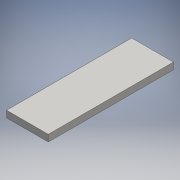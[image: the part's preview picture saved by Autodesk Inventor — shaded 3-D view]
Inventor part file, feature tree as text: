
AUTODESK INVENTOR PART (.ipt)
format: ipt  version: 2016 SP1 (Build 200210100, 210)  size: 88,576 bytes
history: native  units: mm
features: extrude x1, sketch x1
ambient origin geometry x8: Origin, YZ Plane, XZ Plane, XY Plane, X Axis, Y Axis, Z Axis, Center Point
bodies: Solid1 (feature_tree)
feature tree (2):
  extrude  "Extrusion1"  Depth=150.0mm
  sketch  "Sketch1"  dims[d0=50.0mm d1=150.0mm d2=75.0mm d3=25.0mm d4=8.0mm d5=0.0mm]
